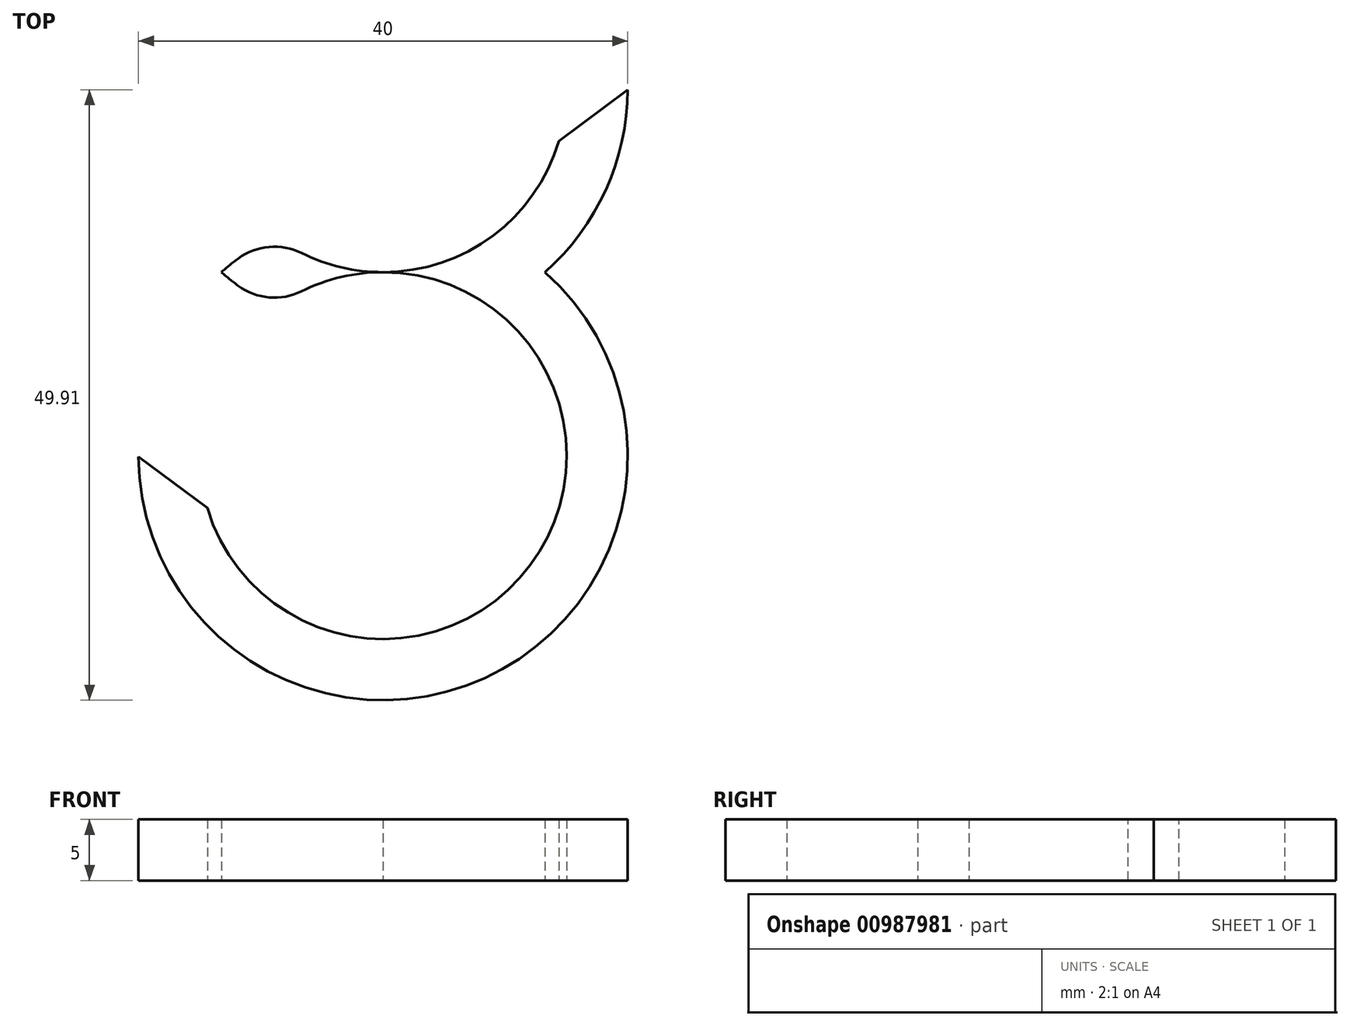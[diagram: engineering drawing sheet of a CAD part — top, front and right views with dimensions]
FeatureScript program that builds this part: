
annotation { "Feature Type Name" : "Feature", "Feature Type Description" : "" }
export const myFeature = defineFeature(function(context is Context, id is Id, definition is map)
    precondition{}
    {
        {
            var Q0;
            Q0=qCreatedBy(makeId("Top.planeOp"),FACE);
            var sketch = newSketch(context, id + "F0", { "sketchPlane" : qUnion([Q0])});
            skLineSegment(sketch, "E0", {"start": v(0, 0) * mm, "end": v(0, 60) * mm});
            skLineSegment(sketch, "E1", {"start": v(0, 60) * mm, "end": v(0, 30) * mm});
            skLineSegment(sketch, "E2", {"start": v(0, 30) * mm, "end": v(0, 15) * mm});
            skLineSegment(sketch, "E3", {"start": v(0, 15) * mm, "end": v(0, 45) * mm});
            skCircle(sketch, "E4", {"center": v(0, 45) * mm, "radius": 15 * mm});
            skCircle(sketch, "E5", {"center": v(0, 15) * mm, "radius": 15 * mm});
            skCircle(sketch, "E6.0", {"center": v(0, 15) * mm, "radius": 20 * mm});
            skCircle(sketch, "E7.0", {"center": v(0, 45) * mm, "radius": 20 * mm});
            skLineSegment(sketch, "E8", {"start": v(0, 15) * mm, "end": v(-20, 15) * mm});
            skLineSegment(sketch, "E9", {"start": v(0, 45) * mm, "end": v(20, 45) * mm});
            skLineSegment(sketch, "E10", {"start": v(8.89, 27.08) * mm, "end": v(-8.89, 27.08) * mm});
            skLineSegment(sketch, "E11", {"start": v(-8.89, 32.92) * mm, "end": v(8.89, 32.92) * mm});
            skSolve(sketch);
        }
        {
            var Q0;
            {var subQ1=sQuery(id+"F0.wireOp",EDGE,"E4");var subQ7=makeQuery(id+"F0.imprint","INTERSECT",VERTEX,{"derivedFrom":[sQuery(id+"F0.wireOp",EDGE,"E1"),subQ1]});Q0=makeQuery(id+"F0.imprint","IMPRINT",FACE,{"disambiguationData":[TD([[makeQuery(id+"F0.imprint","IMPRINT",EDGE,{"disambiguationData":[TD([[subQ7,1.0]])],"derivedFrom":subQ1}),-1.0]])]});}
            var Q1;
            {var subQ0=sQuery(id+"F0.wireOp",EDGE,"E6.0");var subQ5=sQuery(id+"F0.wireOp",EDGE,"E7.0");var subQ7=makeQuery(id+"F0.imprint","INTERSECT",VERTEX,{"disambiguationData":[OD(1.0)],"derivedFrom":[subQ0,subQ5]});Q1=makeQuery(id+"F0.imprint","IMPRINT",FACE,{"disambiguationData":[TD([[makeQuery(id+"F0.imprint","IMPRINT",EDGE,{"disambiguationData":[TD([[subQ7,1.0]])],"derivedFrom":subQ0}),1.0]])]});}
            var Q2;
            {var subQ0=sQuery(id+"F0.wireOp",EDGE,"E11");var subQ1=sQuery(id+"F0.wireOp",EDGE,"E3");var subQ2=makeQuery(id+"F0.imprint","INTERSECT",VERTEX,{"derivedFrom":[subQ1,subQ0]});Q2=makeQuery(id+"F0.imprint","IMPRINT",FACE,{"disambiguationData":[TD([[makeQuery(id+"F0.imprint","IMPRINT",EDGE,{"disambiguationData":[TD([[subQ2,1.0]])],"derivedFrom":subQ1}),1.0]])]});}
            var Q3;
            {var subQ0=sQuery(id+"F0.wireOp",EDGE,"E10");var subQ1=sQuery(id+"F0.wireOp",EDGE,"E3");var subQ2=makeQuery(id+"F0.imprint","INTERSECT",VERTEX,{"derivedFrom":[subQ1,subQ0]});Q3=makeQuery(id+"F0.imprint","IMPRINT",FACE,{"disambiguationData":[TD([[makeQuery(id+"F0.imprint","IMPRINT",EDGE,{"disambiguationData":[TD([[subQ2,-1.0]])],"derivedFrom":subQ1}),1.0]])]});}
            var Q4;
            {var subQ0=sQuery(id+"F0.wireOp",EDGE,"E10");var subQ1=sQuery(id+"F0.wireOp",EDGE,"E3");var subQ2=makeQuery(id+"F0.imprint","INTERSECT",VERTEX,{"derivedFrom":[subQ1,subQ0]});Q4=makeQuery(id+"F0.imprint","IMPRINT",FACE,{"disambiguationData":[TD([[makeQuery(id+"F0.imprint","IMPRINT",EDGE,{"disambiguationData":[TD([[subQ2,-1.0]])],"derivedFrom":subQ1}),-1.0]])]});}
            var Q5;
            {var subQ0=sQuery(id+"F0.wireOp",EDGE,"E11");var subQ1=sQuery(id+"F0.wireOp",EDGE,"E3");var subQ2=makeQuery(id+"F0.imprint","INTERSECT",VERTEX,{"derivedFrom":[subQ1,subQ0]});Q5=makeQuery(id+"F0.imprint","IMPRINT",FACE,{"disambiguationData":[TD([[makeQuery(id+"F0.imprint","IMPRINT",EDGE,{"disambiguationData":[TD([[subQ2,1.0]])],"derivedFrom":subQ1}),-1.0]])]});}
            var Q6;
            {var subQ0=sQuery(id+"F0.wireOp",EDGE,"E6.0");var subQ5=sQuery(id+"F0.wireOp",EDGE,"E7.0");var subQ7=makeQuery(id+"F0.imprint","INTERSECT",VERTEX,{"disambiguationData":[OD(0.0)],"derivedFrom":[subQ0,subQ5]});Q6=makeQuery(id+"F0.imprint","IMPRINT",FACE,{"disambiguationData":[TD([[makeQuery(id+"F0.imprint","IMPRINT",EDGE,{"disambiguationData":[TD([[subQ7,-1.0]])],"derivedFrom":subQ0}),1.0]])]});}
            var Q7;
            {var subQ1=sQuery(id+"F0.wireOp",EDGE,"E5");var subQ5=makeQuery(id+"F0.imprint","INTERSECT",VERTEX,{"derivedFrom":[sQuery(id+"F0.wireOp",EDGE,"E0"),subQ1]});Q7=makeQuery(id+"F0.imprint","IMPRINT",FACE,{"disambiguationData":[TD([[makeQuery(id+"F0.imprint","IMPRINT",EDGE,{"disambiguationData":[TD([[subQ5,1.0]])],"derivedFrom":subQ1}),-1.0]])]});}
            extrude(context, id + "F1", {"entities" : qUnion([Q0, Q1, Q2, Q3, Q4, Q5, Q6, Q7]), "depth" : 5 * mm, "offsetDistance" : 25 * mm});
        }
        {
            var Q0;
            Q0=makeQuery(id+"F1.opExtrude","SWEPT_EDGE",EDGE,{"disambiguationData":[OSD([sQuery(id+"F0.wireOp",EDGE,"E5"),sQuery(id+"F0.wireOp",EDGE,"E8")])]});
            var Q1;
            Q1=makeQuery(id+"F1.opExtrude","SWEPT_EDGE",EDGE,{"disambiguationData":[OSD([sQuery(id+"F0.wireOp",EDGE,"E4"),sQuery(id+"F0.wireOp",EDGE,"E9")])]});
            chamfer(context, id + "F2", {"entities" : qUnion([Q0, Q1]), "width" : 6 * mm, "tangentPropagation" : true});
        }
        {
            var Q0;
            {var subQ0=sQuery(id+"F0.wireOp",EDGE,"E11");var subQ1=sQuery(id+"F0.wireOp",EDGE,"E6.0");var subQ2=sQuery(id+"F0.wireOp",EDGE,"E4");Q0=makeQuery(id+"F1.opExtrude","SWEPT_EDGE",EDGE,{"disambiguationData":[OSD([subQ2,subQ1,subQ0]),TDD([makeQuery(id+"F0.imprint","INTERSECT",VERTEX,{"disambiguationData":[OD(1.0)],"derivedFrom":[subQ2,subQ1,subQ0]})])]});}
            var Q1;
            {var subQ0=sQuery(id+"F0.wireOp",EDGE,"E10");var subQ1=sQuery(id+"F0.wireOp",EDGE,"E7.0");var subQ2=sQuery(id+"F0.wireOp",EDGE,"E5");Q1=makeQuery(id+"F1.opExtrude","SWEPT_EDGE",EDGE,{"disambiguationData":[OSD([subQ2,subQ1,subQ0]),TDD([makeQuery(id+"F0.imprint","INTERSECT",VERTEX,{"disambiguationData":[OD(1.0)],"derivedFrom":[subQ2,subQ1,subQ0]})])]});}
            var Q2;
            {var subQ0=sQuery(id+"F0.wireOp",EDGE,"E10");var subQ1=sQuery(id+"F0.wireOp",EDGE,"E7.0");var subQ2=sQuery(id+"F0.wireOp",EDGE,"E5");Q2=makeQuery(id+"F1.opExtrude","SWEPT_EDGE",EDGE,{"disambiguationData":[OSD([subQ2,subQ1,subQ0]),TDD([makeQuery(id+"F0.imprint","INTERSECT",VERTEX,{"disambiguationData":[OD(0.0)],"derivedFrom":[subQ2,subQ1,subQ0]})])]});}
            var Q3;
            {var subQ0=sQuery(id+"F0.wireOp",EDGE,"E11");var subQ1=sQuery(id+"F0.wireOp",EDGE,"E6.0");var subQ2=sQuery(id+"F0.wireOp",EDGE,"E4");Q3=makeQuery(id+"F1.opExtrude","SWEPT_EDGE",EDGE,{"disambiguationData":[OSD([subQ2,subQ1,subQ0]),TDD([makeQuery(id+"F0.imprint","INTERSECT",VERTEX,{"disambiguationData":[OD(0.0)],"derivedFrom":[subQ2,subQ1,subQ0]})])]});}
            fillet(context, id + "F3", {"entities" : qUnion([Q0, Q1, Q2, Q3]), "radius" : 5 * mm, "tangentPropagation" : true, "allowEdgeOverflow" : false});
        }
    });
